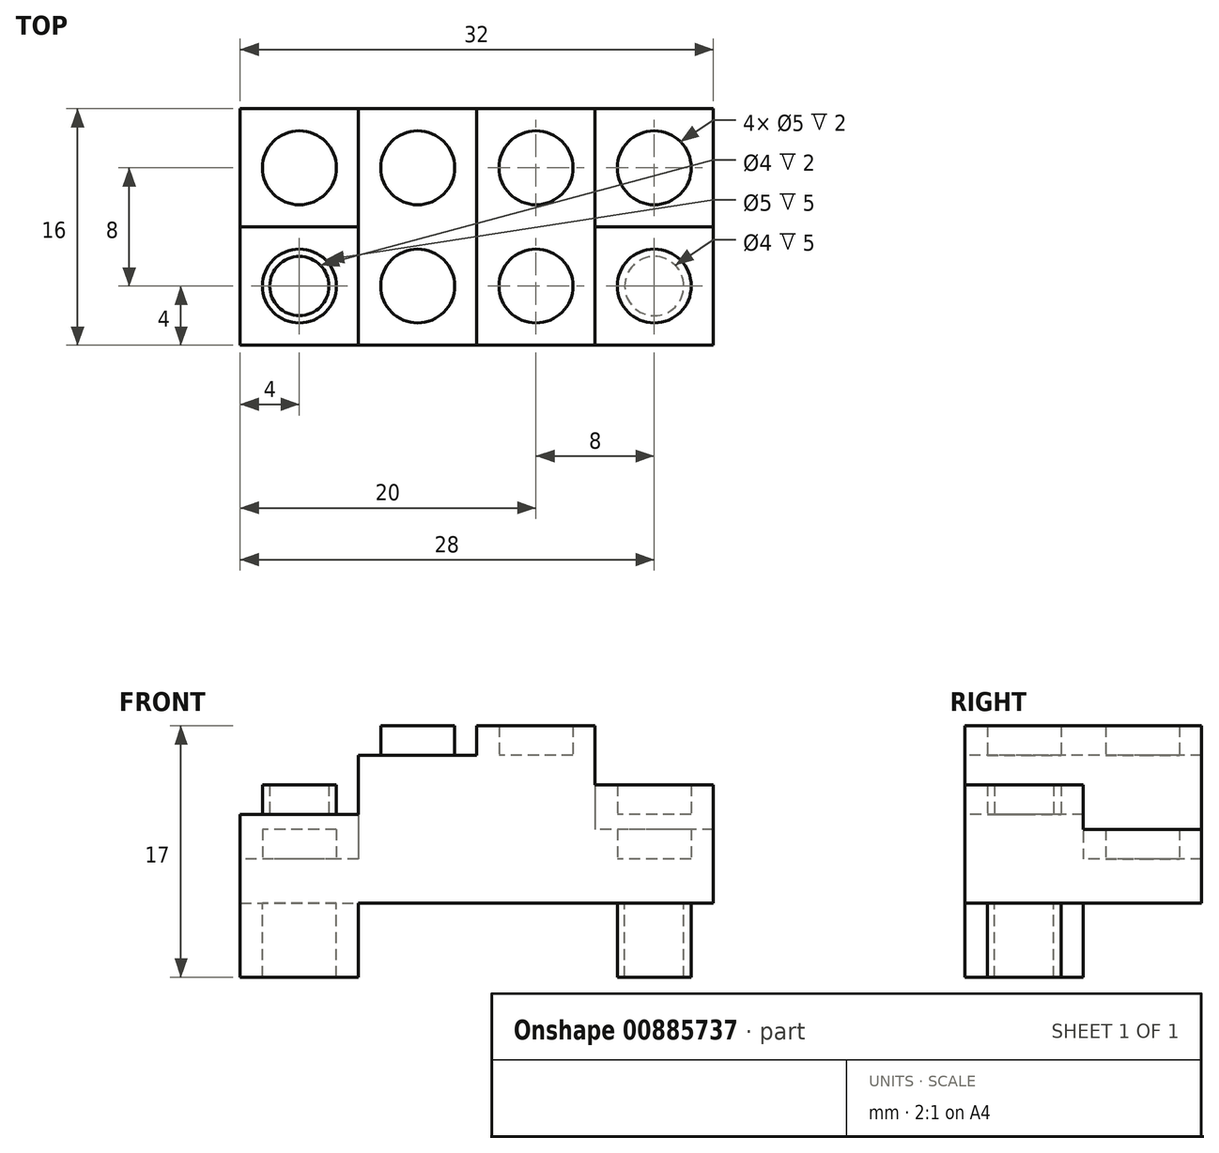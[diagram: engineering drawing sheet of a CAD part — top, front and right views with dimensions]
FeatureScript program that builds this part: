
annotation { "Feature Type Name" : "Feature", "Feature Type Description" : "" }
export const myFeature = defineFeature(function(context is Context, id is Id, definition is map)
    precondition{}
    {
        {
            var Q0;
            Q0=qCreatedBy(makeId("Top.planeOp"),FACE);
            var sketch = newSketch(context, id + "F0", { "sketchPlane" : qUnion([Q0])});
            skLineSegment(sketch, "E0.bottom", {"start": v(16, 8) * mm, "end": v(-16, 8) * mm});
            skLineSegment(sketch, "E0.top", {"start": v(16, -8) * mm, "end": v(-16, -8) * mm});
            skLineSegment(sketch, "E0.left", {"start": v(16, 8) * mm, "end": v(16, -8) * mm});
            skLineSegment(sketch, "E0.right", {"start": v(-16, 8) * mm, "end": v(-16, -8) * mm});
            skCircle(sketch, "E1", {"center": v(-12, -4) * mm, "radius": 2.5 * mm});
            skCircle(sketch, "E2", {"center": v(-12, 4) * mm, "radius": 2.5 * mm});
            skCircle(sketch, "E3", {"center": v(-4, 4) * mm, "radius": 2.5 * mm});
            skCircle(sketch, "E4", {"center": v(-4, -4) * mm, "radius": 2.5 * mm});
            skLineSegment(sketch, "E5.bottom", {"start": v(-16, 8) * mm, "end": v(-8, 8) * mm});
            skLineSegment(sketch, "E5.top", {"start": v(-16, -8) * mm, "end": v(-8, -8) * mm});
            skLineSegment(sketch, "E5.right", {"start": v(-8, 8) * mm, "end": v(-8, -8) * mm});
            skLineSegment(sketch, "E6.bottom", {"start": v(-8, -8) * mm, "end": v(0, -8) * mm});
            skLineSegment(sketch, "E6.top", {"start": v(-8, 8) * mm, "end": v(0, 8) * mm});
            skLineSegment(sketch, "E6.left", {"start": v(-8, -8) * mm, "end": v(-8, 8) * mm});
            skLineSegment(sketch, "E6.right", {"start": v(0, -8) * mm, "end": v(0, 8) * mm});
            skLineSegment(sketch, "E7.MirrorCS", {"start": v(8, -8) * mm, "end": v(8, 8) * mm});
            skCircle(sketch, "E8.MirrorC", {"center": v(4, 4) * mm, "radius": 2.5 * mm});
            skCircle(sketch, "E9.MirrorC", {"center": v(4, -4) * mm, "radius": 2.5 * mm});
            skCircle(sketch, "E10.MirrorC", {"center": v(12, -4) * mm, "radius": 2.5 * mm});
            skCircle(sketch, "E11.MirrorC", {"center": v(12, 4) * mm, "radius": 2.5 * mm});
            skCircle(sketch, "E12", {"center": v(-12, -4) * mm, "radius": 2 * mm});
            skCircle(sketch, "E13", {"center": v(12, -4) * mm, "radius": 2 * mm});
            skLineSegment(sketch, "E14", {"start": v(-16, 0) * mm, "end": v(16, 0) * mm});
            skSolve(sketch);
        }
        {
            var Q0;
            Q0=makeQuery(id+"F0.imprint","IMPRINT",FACE,{"disambiguationData":[TD([[makeQuery(id+"F0.imprint","IMPRINT",EDGE,{"derivedFrom":sQuery(id+"F0.wireOp",EDGE,"E3")}),-1.0]])]});
            var Q1;
            Q1=makeQuery(id+"F0.imprint","IMPRINT",FACE,{"disambiguationData":[TD([[makeQuery(id+"F0.imprint","IMPRINT",EDGE,{"derivedFrom":sQuery(id+"F0.wireOp",EDGE,"E8.MirrorC")}),1.0]])]});
            var Q2;
            Q2=makeQuery(id+"F0.imprint","IMPRINT",FACE,{"disambiguationData":[TD([[makeQuery(id+"F0.imprint","IMPRINT",EDGE,{"derivedFrom":sQuery(id+"F0.wireOp",EDGE,"E4")}),-1.0]])]});
            var Q3;
            Q3=makeQuery(id+"F0.imprint","IMPRINT",FACE,{"disambiguationData":[TD([[makeQuery(id+"F0.imprint","IMPRINT",EDGE,{"derivedFrom":sQuery(id+"F0.wireOp",EDGE,"E9.MirrorC")}),1.0]])]});
            extrude(context, id + "F1", {"entities" : qUnion([Q0, Q1, Q2, Q3]), "depth" : 10 * mm, "offsetDistance" : 25 * mm});
        }
        {
            var Q0;
            Q0=makeQuery(id+"F0.imprint","IMPRINT",FACE,{"disambiguationData":[TD([[makeQuery(id+"F0.imprint","IMPRINT",EDGE,{"derivedFrom":sQuery(id+"F0.wireOp",EDGE,"E3")}),1.0]])]});
            var Q1;
            Q1=makeQuery(id+"F0.imprint","IMPRINT",FACE,{"disambiguationData":[TD([[makeQuery(id+"F0.imprint","IMPRINT",EDGE,{"derivedFrom":sQuery(id+"F0.wireOp",EDGE,"E8.MirrorC")}),-1.0]])]});
            var Q2;
            Q2=makeQuery(id+"F0.imprint","IMPRINT",FACE,{"disambiguationData":[TD([[makeQuery(id+"F0.imprint","IMPRINT",EDGE,{"derivedFrom":sQuery(id+"F0.wireOp",EDGE,"E4")}),1.0]])]});
            var Q3;
            Q3=makeQuery(id+"F0.imprint","IMPRINT",FACE,{"disambiguationData":[TD([[makeQuery(id+"F0.imprint","IMPRINT",EDGE,{"derivedFrom":sQuery(id+"F0.wireOp",EDGE,"E9.MirrorC")}),-1.0]])]});
            extrude(context, id + "F2", {"entities" : qUnion([Q0, Q1, Q2, Q3]), "operationType" : NewBodyOperationType.ADD, "depth" : 12 * mm, "offsetDistance" : 25 * mm});
        }
        {
            var Q0;
            Q0=makeQuery(id+"F0.imprint","IMPRINT",FACE,{"disambiguationData":[TD([[makeQuery(id+"F0.imprint","IMPRINT",EDGE,{"derivedFrom":sQuery(id+"F0.wireOp",EDGE,"E2")}),-1.0]])]});
            var Q1;
            Q1=makeQuery(id+"F0.imprint","IMPRINT",FACE,{"disambiguationData":[TD([[makeQuery(id+"F0.imprint","IMPRINT",EDGE,{"derivedFrom":sQuery(id+"F0.wireOp",EDGE,"E11.MirrorC")}),1.0]])]});
            extrude(context, id + "F3", {"entities" : qUnion([Q0, Q1]), "operationType" : NewBodyOperationType.ADD, "depth" : 3 * mm, "offsetDistance" : 25 * mm});
        }
        {
            var Q0;
            Q0=makeQuery(id+"F0.imprint","IMPRINT",FACE,{"disambiguationData":[TD([[makeQuery(id+"F0.imprint","IMPRINT",EDGE,{"derivedFrom":sQuery(id+"F0.wireOp",EDGE,"E2")}),1.0]])]});
            var Q1;
            Q1=makeQuery(id+"F0.imprint","IMPRINT",FACE,{"disambiguationData":[TD([[makeQuery(id+"F0.imprint","IMPRINT",EDGE,{"derivedFrom":sQuery(id+"F0.wireOp",EDGE,"E11.MirrorC")}),-1.0]])]});
            extrude(context, id + "F4", {"entities" : qUnion([Q0, Q1]), "operationType" : NewBodyOperationType.ADD, "depth" : 5 * mm, "offsetDistance" : 25 * mm});
        }
        {
            var Q0;
            Q0=makeQuery(id+"F0.imprint","IMPRINT",FACE,{"disambiguationData":[TD([[makeQuery(id+"F0.imprint","IMPRINT",EDGE,{"derivedFrom":sQuery(id+"F0.wireOp",EDGE,"E1")}),-1.0]])]});
            var Q1;
            Q1=makeQuery(id+"F0.imprint","IMPRINT",FACE,{"disambiguationData":[TD([[makeQuery(id+"F0.imprint","IMPRINT",EDGE,{"derivedFrom":sQuery(id+"F0.wireOp",EDGE,"E10.MirrorC")}),1.0]])]});
            extrude(context, id + "F5", {"entities" : qUnion([Q0, Q1]), "operationType" : NewBodyOperationType.ADD, "depth" : 6 * mm, "offsetDistance" : 25 * mm});
        }
        {
            var Q0;
            Q0=makeQuery(id+"F0.imprint","IMPRINT",FACE,{"disambiguationData":[TD([[makeQuery(id+"F0.imprint","IMPRINT",EDGE,{"derivedFrom":sQuery(id+"F0.wireOp",EDGE,"E1")}),1.0]])]});
            var Q1;
            Q1=makeQuery(id+"F0.imprint","IMPRINT",FACE,{"disambiguationData":[TD([[makeQuery(id+"F0.imprint","IMPRINT",EDGE,{"derivedFrom":sQuery(id+"F0.wireOp",EDGE,"E10.MirrorC")}),-1.0]])]});
            extrude(context, id + "F6", {"entities" : qUnion([Q0, Q1]), "operationType" : NewBodyOperationType.ADD, "depth" : 8 * mm, "offsetDistance" : 25 * mm});
        }
        {
            var Q0;
            Q0=makeQuery(id+"F0.imprint","IMPRINT",FACE,{"disambiguationData":[TD([[makeQuery(id+"F0.imprint","IMPRINT",EDGE,{"derivedFrom":sQuery(id+"F0.wireOp",EDGE,"E12")}),1.0]])]});
            var Q1;
            Q1=makeQuery(id+"F0.imprint","IMPRINT",FACE,{"disambiguationData":[TD([[makeQuery(id+"F0.imprint","IMPRINT",EDGE,{"derivedFrom":sQuery(id+"F0.wireOp",EDGE,"E13")}),1.0]])]});
            extrude(context, id + "F7", {"entities" : qUnion([Q0, Q1]), "operationType" : NewBodyOperationType.ADD, "depth" : 6 * mm, "offsetDistance" : 25 * mm});
        }
        {
            var Q0;
            Q0=makeQuery(id+"F0.imprint","IMPRINT",FACE,{"disambiguationData":[TD([[makeQuery(id+"F0.imprint","IMPRINT",EDGE,{"derivedFrom":sQuery(id+"F0.wireOp",EDGE,"E1")}),-1.0]])]});
            var Q1;
            Q1=makeQuery(id+"F0.imprint","IMPRINT",FACE,{"disambiguationData":[TD([[makeQuery(id+"F0.imprint","IMPRINT",EDGE,{"derivedFrom":sQuery(id+"F0.wireOp",EDGE,"E10.MirrorC")}),1.0]])]});
            extrude(context, id + "F8", {"entities" : qUnion([Q0, Q1]), "operationType" : NewBodyOperationType.ADD, "oppositeDirection" : true, "depth" : 5 * mm, "offsetDistance" : 25 * mm});
        }
    });
